# Revit family: Patio-Door_650_4-Light_OXXO_Novatech
name_source: partatom
category: Doors
units: mm (PartAtom-declared; Revit-internal decimal feet)

## family parameters
Always vertical = Yes
Classification Number = 23.30.10.00
Cut with Voids When Loaded = No
Host = Wall
Room Calculation Point = No
Shared = No

## types (5) — shared parameters
Analytic Construction = <None>
CAD Details = https://www.arcat.com
Define Thermal Properties by = Schematic Type
Frame Material = Aluminum
Function = Interior
Handle Height = 38"
Hardware Material = Aluminum
Keynote = 08 32 00
Look Handle = Yes
Manufacturer = Novatech
Model = 650
Panel Material = Glass
Product Page URL = https://www.arcat.com
Specification = https://www.arcat.com
Thickness = 5 3/4"
URL = https://www.groupenovatech.com
View Handle = Yes
Wall Closure = By host

## per-type parameters (varying)
| type | Height | Height Sash O | Height Sash X | Model_Sash to Reference Line | Rough Height | Rough Width | Width | Width Sash O | Width Sash X |
| 116 7/16"W X 79 1/2"H | 79 1/2" | 75 7/8" | 75 7/8" | 28 1/2" | 80" | 117" | 116 1/2" | 29 3/4" | 29 3/4" |
| 140 1/2"W X 79 1/2"H | 79 1/2" | 75 7/8" | 75 7/8" | 34 1/2" | 80" | 141" | 140 1/2" | 35 3/4" | 35 3/4" |
| 188 3/8"W X 79 1/2"H | 79 1/2" | 75 7/8" | 75 7/8" | 46 1/2" | 80" | 188 7/8" | 188 3/8" | 47 3/4" | 47 3/4" |
| 140 1/2"W X 95 1/2"H | 95 1/2" | 91 7/8" | 91 7/8" | 34 1/2" | 96" | 141" | 140 1/2" | 35 3/4" | 35 3/4" |
| 188 3/8"W X 95 1/2"H | 95 1/2" | 91 7/8" | 91 7/8" | 46 1/2" | 96" | 188 7/8" | 188 3/8" | 47 3/4" | 47 3/4" |

## geometry (parser evidence)
native form markers: Sweep x91
no freeform markers — native parametric forms only
